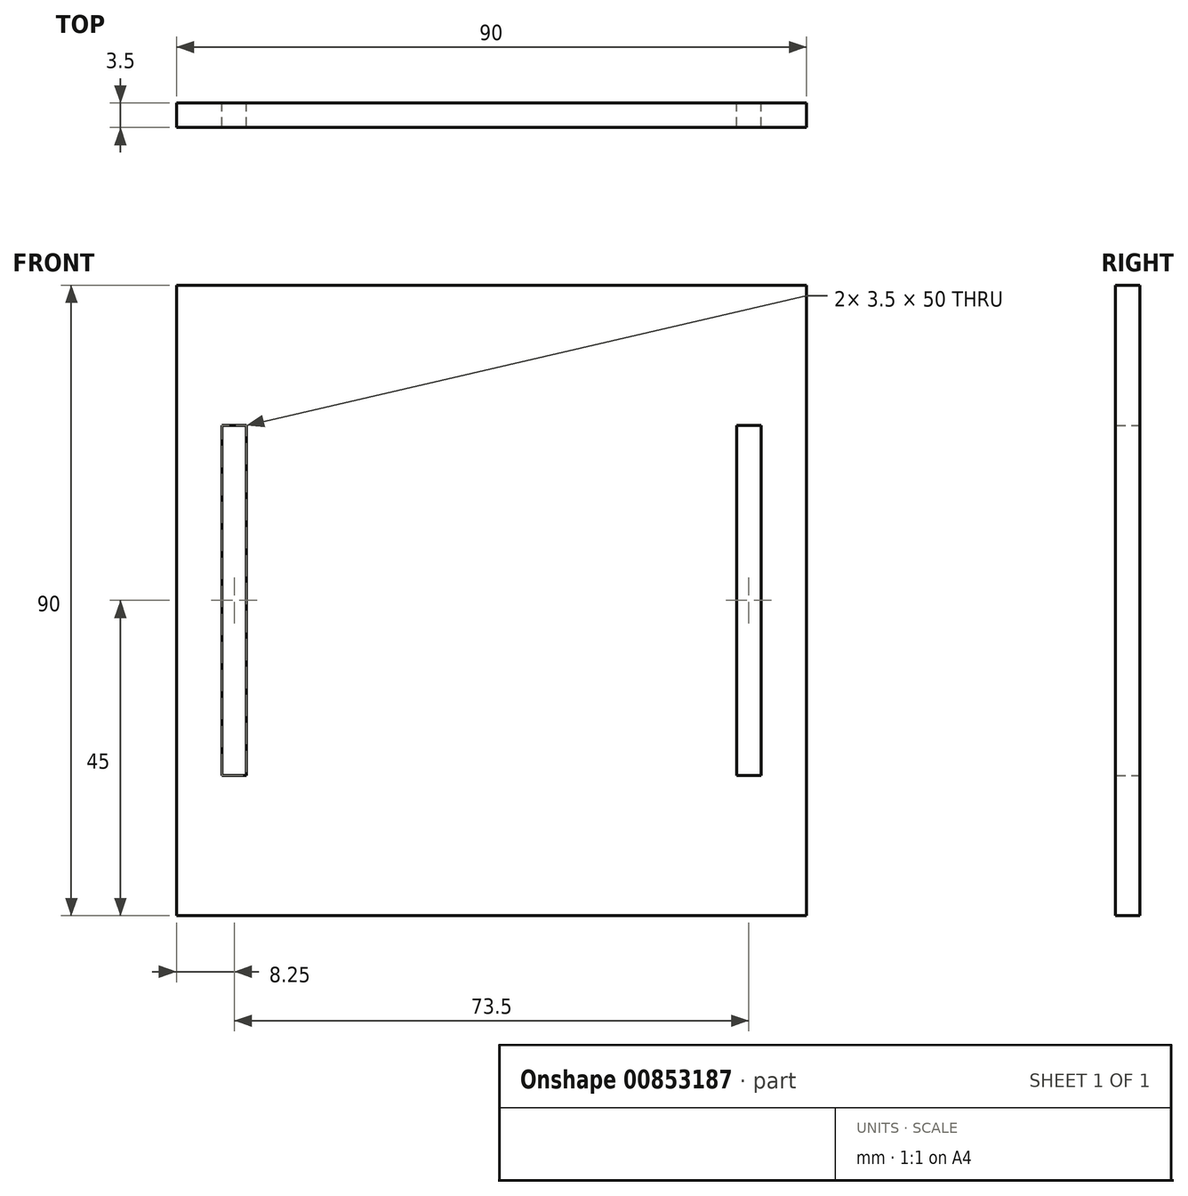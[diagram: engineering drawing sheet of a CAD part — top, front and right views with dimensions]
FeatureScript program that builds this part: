
annotation { "Feature Type Name" : "Feature", "Feature Type Description" : "" }
export const myFeature = defineFeature(function(context is Context, id is Id, definition is map)
    precondition{}
    {
        {
            var Q0;
            Q0=qCreatedBy(makeId("Front.planeOp"),FACE);
            var sketch = newSketch(context, id + "F0", { "sketchPlane" : qUnion([Q0])});
            skLineSegment(sketch, "E0", {"start": v(0, 0) * mm, "end": v(0, -45) * mm});
            skLineSegment(sketch, "E1", {"start": v(0, 0) * mm, "end": v(45, 0) * mm});
            skLineSegment(sketch, "E2.0", {"start": v(45, 0) * mm, "end": v(45, -45) * mm});
            skLineSegment(sketch, "E3.0", {"start": v(0, -45) * mm, "end": v(45, -45) * mm});
            skLineSegment(sketch, "E4.0", {"start": v(35, -25) * mm, "end": v(38.5, -25) * mm});
            skLineSegment(sketch, "E5.0", {"start": v(35, 0) * mm, "end": v(35, -25) * mm});
            skLineSegment(sketch, "E6.0", {"start": v(38.5, 0) * mm, "end": v(38.5, -25) * mm});
            skLineSegment(sketch, "E7.MirrorCS", {"start": v(35, 25) * mm, "end": v(38.5, 25) * mm});
            skLineSegment(sketch, "E8.MirrorCS", {"start": v(38.5, 0) * mm, "end": v(38.5, 25) * mm});
            skLineSegment(sketch, "E9.MirrorCS", {"start": v(35, 0) * mm, "end": v(35, 25) * mm});
            skLineSegment(sketch, "E10.MirrorCS", {"start": v(45, 0) * mm, "end": v(45, 45) * mm});
            skLineSegment(sketch, "E11.MirrorCS", {"start": v(0, 45) * mm, "end": v(45, 45) * mm});
            skLineSegment(sketch, "E12.MirrorCS", {"start": v(0, 0) * mm, "end": v(0, 45) * mm});
            skLineSegment(sketch, "E13.MirrorCS", {"start": v(-38.5, 0) * mm, "end": v(-38.5, -25) * mm});
            skLineSegment(sketch, "E14.MirrorCS", {"start": v(-35, -25) * mm, "end": v(-38.5, -25) * mm});
            skLineSegment(sketch, "E15.MirrorCS", {"start": v(-35, 25) * mm, "end": v(-38.5, 25) * mm});
            skLineSegment(sketch, "E16.MirrorCS", {"start": v(-38.5, 0) * mm, "end": v(-38.5, 25) * mm});
            skLineSegment(sketch, "E17.MirrorCS", {"start": v(-45, 0) * mm, "end": v(-45, -45) * mm});
            skLineSegment(sketch, "E18.MirrorCS", {"start": v(0, -45) * mm, "end": v(-45, -45) * mm});
            skLineSegment(sketch, "E19.MirrorCS", {"start": v(-35, 0) * mm, "end": v(-35, 25) * mm});
            skLineSegment(sketch, "E20.MirrorCS", {"start": v(-35, 0) * mm, "end": v(-35, -25) * mm});
            skLineSegment(sketch, "E21.MirrorCS", {"start": v(0, 45) * mm, "end": v(-45, 45) * mm});
            skLineSegment(sketch, "E22.MirrorCS", {"start": v(-45, 0) * mm, "end": v(-45, 45) * mm});
            skLineSegment(sketch, "E23.MirrorCS", {"start": v(0, 0) * mm, "end": v(-45, 0) * mm});
            skSolve(sketch);
        }
        {
            var Q0;
            Q0 = qSketchRegion(id + "F0", true);
            extrude(context, id + "F1", {"entities" : qUnion([Q0]), "depth" : 3.5 * mm, "offsetDistance" : 25 * mm});
        }
    });
